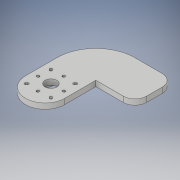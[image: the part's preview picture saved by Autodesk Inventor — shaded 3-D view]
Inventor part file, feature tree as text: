
AUTODESK INVENTOR PART (.ipt)
format: ipt  version: 2019 (Build 230136000, 136)  size: 232,448 bytes
history: native  units: mm
features: extrude x6, sketch x6, fillet x2
ambient origin geometry x8: Origin, YZ Plane, XZ Plane, XY Plane, X Axis, Y Axis, Z Axis, Center Point
bodies: Solid1 (feature_tree)
feature tree (14):
  extrude  "Extrusion1"  Depth=100.0mm
  extrude  "Extrusion2"  Depth=7.0mm TaperAngle=0.0deg
  fillet  "Fillet1"  Radius=25.0mm
  extrude  "Extrusion3"  Depth=15.0mm
  fillet  "Fillet2"  Radius=44.0mm
  extrude  "Extrusion4"  Depth=44.0mm
  extrude  "Extrusion5"  Depth=3.15mm
  extrude  "Extrusion6"  Depth=3.15mm
  sketch  "Sketch1"  dims[d0=100.0mm d1=130.0mm]
  sketch  "Sketch2"  dims[d2=7.0mm d3=0.0mm d4=7.0mm d5=0.0mm d14=25.0mm]
  sketch  "Sketch5"  dims[d15=7.0mm d16=0.0mm d17=15.0mm d18=44.0mm]
  sketch  "Sketch6"  dims[d19=44.0mm d20=44.0mm]
  sketch  "Sketch7"  dims[d21=0.75mm d22=3.15mm]
  sketch  "Sketch8"  dims[d23=0.75mm d24=3.15mm d25=0.75mm d26=3.15mm d27=0.75mm d28=3.15mm d29=33.0mm d30=0.25mm d31=3.15mm d32=0.25mm d33=3.15mm d34=0.25mm d35=3.15mm d36=0.25mm d37=3.15mm d38=15.0mm d39=7.0mm d40=0.0mm d41=55.0mm d42=7.0mm d43=0.0mm d44=7.0mm d45=0.0mm]
